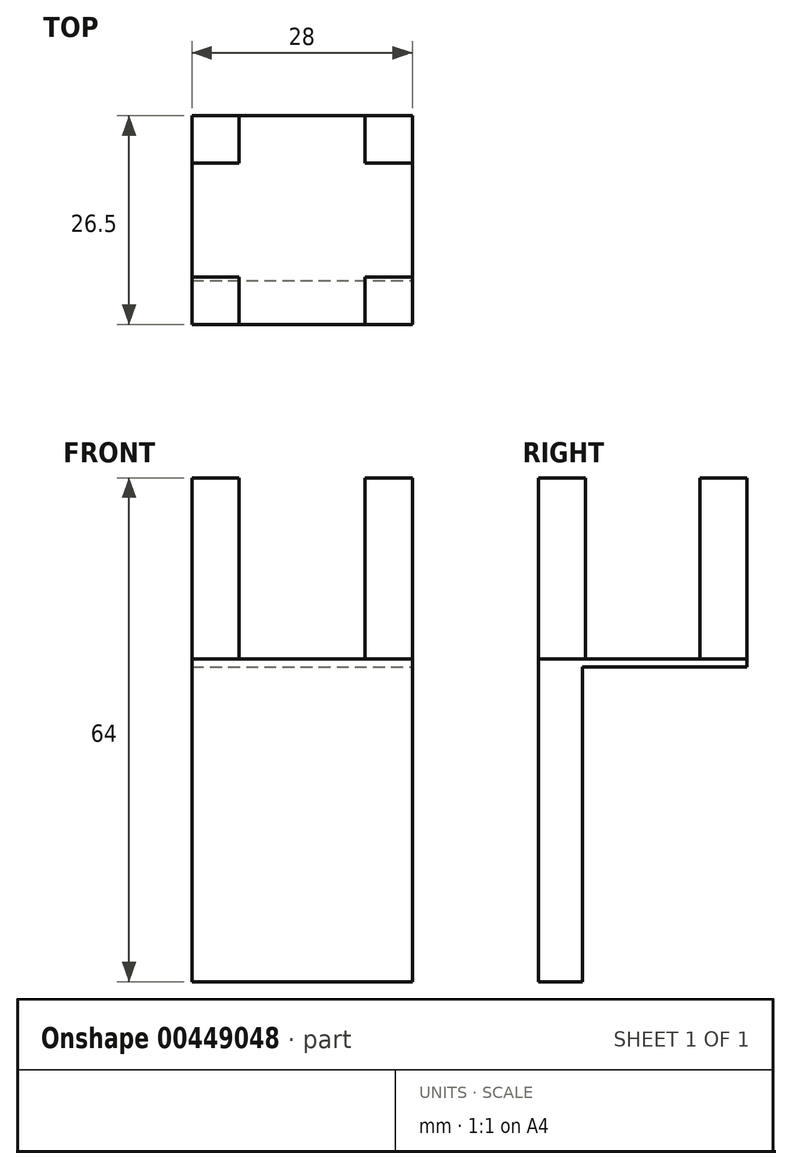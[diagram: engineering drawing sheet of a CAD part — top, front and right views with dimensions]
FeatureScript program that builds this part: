
annotation { "Feature Type Name" : "Feature", "Feature Type Description" : "" }
export const myFeature = defineFeature(function(context is Context, id is Id, definition is map)
    precondition{}
    {
        {
            var Q0;
            Q0=qCreatedBy(makeId("Top.planeOp"),FACE);
            var sketch = newSketch(context, id + "F0", { "sketchPlane" : qUnion([Q0])});
            skLineSegment(sketch, "E0.bottom", {"start": v(0, 0) * mm, "end": v(6, 0) * mm});
            skLineSegment(sketch, "E0.top", {"start": v(0, 6) * mm, "end": v(6, 6) * mm});
            skLineSegment(sketch, "E0.left", {"start": v(0, 0) * mm, "end": v(0, 6) * mm});
            skLineSegment(sketch, "E0.right", {"start": v(6, 0) * mm, "end": v(6, 6) * mm});
            skLineSegment(sketch, "E1.0.1.0", {"start": v(0, 20.5) * mm, "end": v(0, 26.5) * mm});
            skLineSegment(sketch, "E1.0.1.1", {"start": v(0, 20.5) * mm, "end": v(6, 20.5) * mm});
            skLineSegment(sketch, "E1.0.1.2", {"start": v(0, 26.5) * mm, "end": v(6, 26.5) * mm});
            skLineSegment(sketch, "E1.0.1.3", {"start": v(6, 20.5) * mm, "end": v(6, 26.5) * mm});
            skLineSegment(sketch, "E1.1.0.0", {"start": v(22, 0) * mm, "end": v(22, 6) * mm});
            skLineSegment(sketch, "E1.1.0.1", {"start": v(22, 0) * mm, "end": v(28, 0) * mm});
            skLineSegment(sketch, "E1.1.0.2", {"start": v(22, 6) * mm, "end": v(28, 6) * mm});
            skLineSegment(sketch, "E1.1.0.3", {"start": v(28, 0) * mm, "end": v(28, 6) * mm});
            skLineSegment(sketch, "E1.1.1.0", {"start": v(22, 20.5) * mm, "end": v(22, 26.5) * mm});
            skLineSegment(sketch, "E1.1.1.1", {"start": v(22, 20.5) * mm, "end": v(28, 20.5) * mm});
            skLineSegment(sketch, "E1.1.1.2", {"start": v(22, 26.5) * mm, "end": v(28, 26.5) * mm});
            skLineSegment(sketch, "E1.1.1.3", {"start": v(28, 20.5) * mm, "end": v(28, 26.5) * mm});
            skLineSegment(sketch, "E1.direction1", {"start": v(0, 0) * mm, "end": v(22, 0) * mm, "construction": true});
            skLineSegment(sketch, "E1.direction2", {"start": v(0, 0) * mm, "end": v(0, 20.5) * mm, "construction": true});
            skSolve(sketch);
        }
        {
            var Q0;
            Q0 = qSketchRegion(id + "F0", true);
            extrude(context, id + "F1", {"entities" : qUnion([Q0]), "depth" : 23 * mm});
        }
        {
            var Q0;
            Q0=qCreatedBy(makeId("Top.planeOp"),FACE);
            var sketch = newSketch(context, id + "F2", { "sketchPlane" : qUnion([Q0])});
            skLineSegment(sketch, "E2.bottom", {"start": v(0, 0) * mm, "end": v(28, 0) * mm});
            skLineSegment(sketch, "E2.top", {"start": v(0, 26.5) * mm, "end": v(28, 26.5) * mm});
            skLineSegment(sketch, "E2.left", {"start": v(0, 0) * mm, "end": v(0, 26.5) * mm});
            skLineSegment(sketch, "E2.right", {"start": v(28, 0) * mm, "end": v(28, 26.5) * mm});
            skSolve(sketch);
        }
        {
            var Q0;
            Q0=makeQuery(id+"F2.imprint","IMPRINT",FACE,{"disambiguationData":[TD([[makeQuery(id+"F2.imprint","IMPRINT",EDGE,{"derivedFrom":sQuery(id+"F2.wireOp",EDGE,"E2.bottom")}),1.0]])]});
            extrude(context, id + "F3", {"entities" : qUnion([Q0]), "oppositeDirection" : true, "depth" : 1 * mm});
        }
        {
            var Q0;
            Q0=makeQuery(id+"F3.opExtrude","CAP_FACE",FACE,{"disambiguationData":[OSD([sQuery(id+"F2.wireOp",EDGE,"E2.bottom"),sQuery(id+"F2.wireOp",EDGE,"E2.top"),sQuery(id+"F2.wireOp",EDGE,"E2.left"),sQuery(id+"F2.wireOp",EDGE,"E2.right")])],"isStart":false});
            var sketch = newSketch(context, id + "F4", { "sketchPlane" : qUnion([Q0])});
            skLineSegment(sketch, "E3.bottom", {"start": v(0, 0) * mm, "end": v(28, 0) * mm});
            skLineSegment(sketch, "E3.top", {"start": v(0, -5.6) * mm, "end": v(28, -5.6) * mm});
            skLineSegment(sketch, "E3.left", {"start": v(0, 0) * mm, "end": v(0, -5.6) * mm});
            skLineSegment(sketch, "E3.right", {"start": v(28, 0) * mm, "end": v(28, -5.6) * mm});
            skSolve(sketch);
        }
        {
            var Q0;
            Q0=makeQuery(id+"F4.imprint","IMPRINT",FACE,{"disambiguationData":[TD([[makeQuery(id+"F4.imprint","IMPRINT",EDGE,{"derivedFrom":sQuery(id+"F4.wireOp",EDGE,"E3.bottom")}),-1.0]])]});
            extrude(context, id + "F5", {"entities" : qUnion([Q0]), "operationType" : NewBodyOperationType.ADD, "depth" : 40 * mm});
        }
    });
